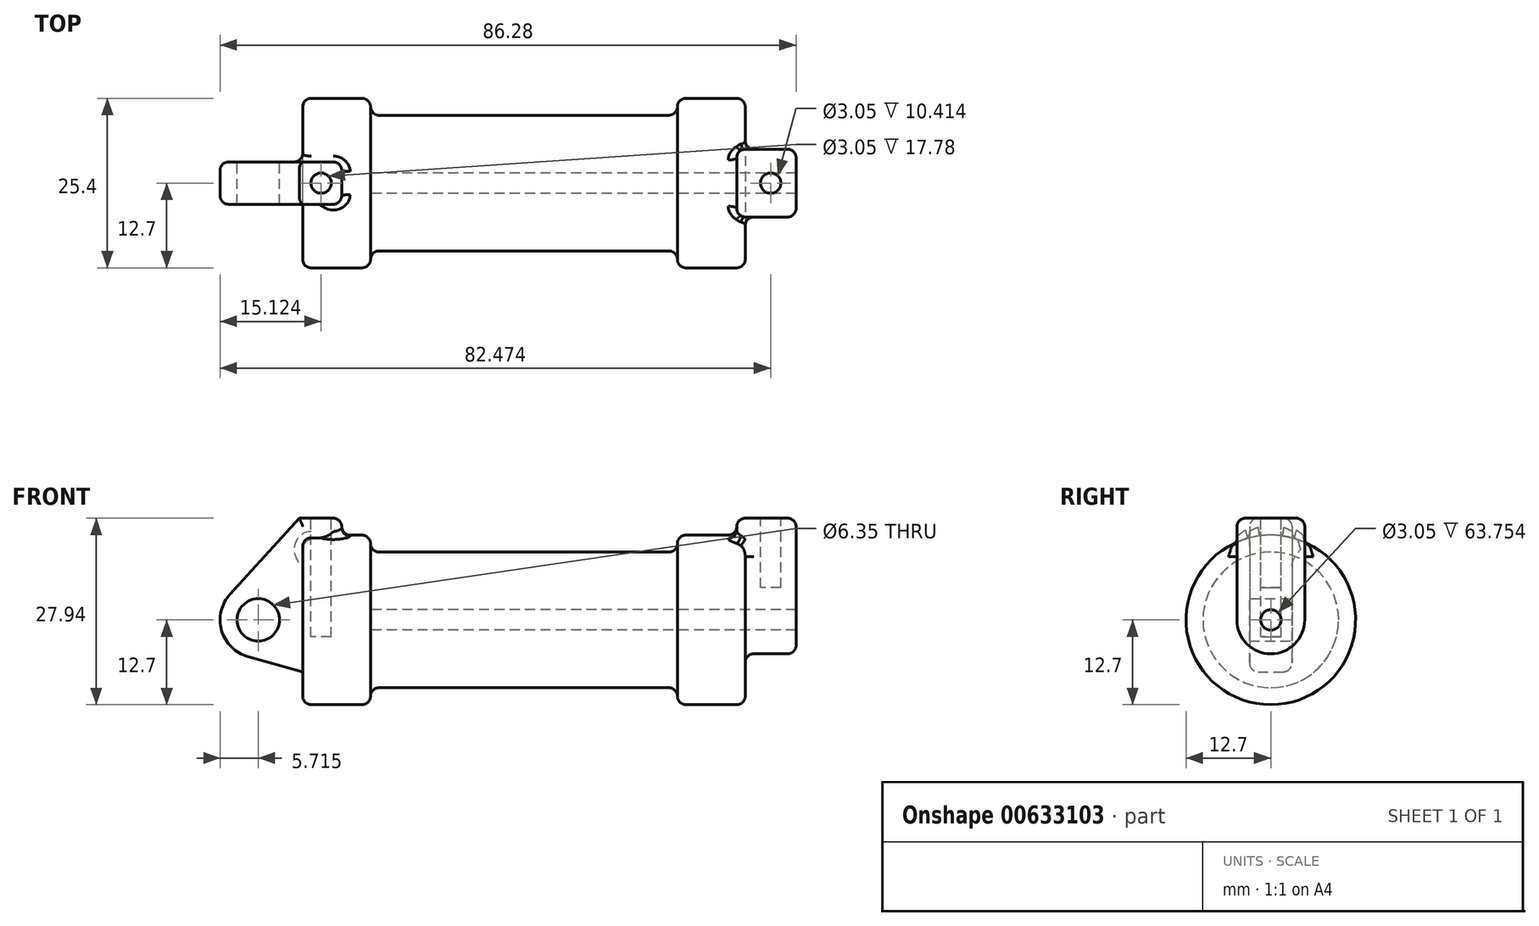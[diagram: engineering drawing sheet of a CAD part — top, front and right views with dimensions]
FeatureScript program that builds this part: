
annotation { "Feature Type Name" : "Feature", "Feature Type Description" : "" }
export const myFeature = defineFeature(function(context is Context, id is Id, definition is map)
    precondition{}
    {
        {
            var Q0;
            Q0=qCreatedBy(makeId("Front.planeOp"),FACE);
            var sketch = newSketch(context, id + "F0", { "sketchPlane" : qUnion([Q0])});
            skLineSegment(sketch, "E0", {"start": v(0, 0) * mm, "end": v(0, 12.7) * mm});
            skLineSegment(sketch, "E1", {"start": v(0, 12.7) * mm, "end": v(10.16, 12.7) * mm});
            skLineSegment(sketch, "E2", {"start": v(10.16, 12.7) * mm, "end": v(10.16, 10.16) * mm});
            skLineSegment(sketch, "E3", {"start": v(10.16, 10.16) * mm, "end": v(56.13, 10.16) * mm});
            skLineSegment(sketch, "E4", {"start": v(56.13, 10.16) * mm, "end": v(56.13, 12.7) * mm});
            skLineSegment(sketch, "E5", {"start": v(56.13, 12.7) * mm, "end": v(66.3, 12.7) * mm});
            skLineSegment(sketch, "E6", {"start": v(66.3, 12.7) * mm, "end": v(66.3, 0) * mm});
            skLineSegment(sketch, "E7", {"start": v(66.3, 0) * mm, "end": v(0, 0) * mm});
            skLineSegment(sketch, "E8", {"start": v(5.84, 15.24) * mm, "end": v(-0.5, 15.24) * mm});
            skLineSegment(sketch, "E9", {"start": v(-0.5, 15.24) * mm, "end": v(-10.88, 3.85) * mm});
            skLineSegment(sketch, "E10", {"start": v(0, 0) * mm, "end": v(-6.65, 0) * mm});
            skCircle(sketch, "E11", {"center": v(-6.65, 0) * mm, "radius": 5.72 * mm});
            skCircle(sketch, "E12", {"center": v(-6.65, 0) * mm, "radius": 3.18 * mm});
            skLineSegment(sketch, "E13", {"start": v(5.84, 15.24) * mm, "end": v(5.84, -9.4) * mm});
            skLineSegment(sketch, "E14", {"start": v(5.84, -9.4) * mm, "end": v(-8.18, -5.5) * mm});
            skSolve(sketch);
        }
        {
            var Q0;
            {var subQ0=sQuery(id+"F0.wireOp",EDGE,"E0");Q0=makeQuery(id+"F0.imprint","IMPRINT",FACE,{"disambiguationData":[TD([[makeQuery(id+"F0.imprint","IMPRINT",EDGE,{"derivedFrom":subQ0}),-1.0]])]});}
            var Q1;
            {var subQ0=sQuery(id+"F0.wireOp",EDGE,"E2");Q1=makeQuery(id+"F0.imprint","IMPRINT",FACE,{"disambiguationData":[TD([[makeQuery(id+"F0.imprint","IMPRINT",EDGE,{"derivedFrom":subQ0}),-1.0]])]});}
            var Q2;
            Q2=sQuery(id+"F0.wireOp",EDGE,"E7");
            revolve(context, id + "F1", {"entities" : qUnion([Q0, Q1]), "axis" : qUnion([Q2]), "revolveType" : RevolveType.FULL});
        }
        {
            var Q0;
            Q0=makeQuery(id+"F1.opRevolve","SWEPT_FACE",FACE,{"disambiguationData":[OSD([sQuery(id+"F0.wireOp",EDGE,"E6")])]});
            var sketch = newSketch(context, id + "F2", { "sketchPlane" : qUnion([Q0])});
            skCircle(sketch, "E15", {"center": v(0, 0) * mm, "radius": 1.52 * mm});
            skCircle(sketch, "E16", {"center": v(0, 0) * mm, "radius": 5.08 * mm});
            skLineSegment(sketch, "E17", {"start": v(5.08, 0) * mm, "end": v(5.08, 15.24) * mm});
            skLineSegment(sketch, "E18", {"start": v(-5.08, 0) * mm, "end": v(-5.08, 15.24) * mm});
            skLineSegment(sketch, "E19", {"start": v(-5.08, 15.24) * mm, "end": v(5.08, 15.24) * mm});
            skSolve(sketch);
        }
        {
            var Q0;
            Q0 = qSketchRegion(id + "F2", true);
            extrude(context, id + "F3", {"entities" : qUnion([Q0]), "operationType" : NewBodyOperationType.ADD, "depth" : 7.62 * mm, "offsetDistance" : 25.4 * mm, "hasSecondDirection" : true, "secondDirectionOppositeDirection" : true, "secondDirectionDepth" : 1.27 * mm});
        }
        {
            var Q0;
            Q0=makeQuery(id+"F2.imprint","IMPRINT",FACE,{"disambiguationData":[TD([[makeQuery(id+"F2.imprint","IMPRINT",EDGE,{"derivedFrom":sQuery(id+"F2.wireOp",EDGE,"E15")}),1.0]])]});
            var Q1;
            Q1=makeQuery(id+"F1.opRevolve","SWEPT_FACE",FACE,{"disambiguationData":[OSD([sQuery(id+"F0.wireOp",EDGE,"E2")])]});
            extrude(context, id + "F4", {"entities" : qUnion([Q0]), "operationType" : NewBodyOperationType.REMOVE, "endBound" : BoundingType.UP_TO_SURFACE, "oppositeDirection" : true, "depth" : 25.4 * mm, "endBoundEntityFace" : qUnion([Q1]), "offsetDistance" : 25.4 * mm});
        }
        {
            var Q0;
            Q0=makeQuery(id+"F3.opExtrude","SWEPT_FACE",FACE,{"disambiguationData":[OSD([sQuery(id+"F2.wireOp",EDGE,"E19")])]});
            var sketch = newSketch(context, id + "F5", { "sketchPlane" : qUnion([Q0])});
            skCircle(sketch, "E20", {"center": v(70.1, 0) * mm, "radius": 1.52 * mm});
            skSolve(sketch);
        }
        {
            var Q0;
            Q0 = qSketchRegion(id + "F5", true);
            extrude(context, id + "F6", {"entities" : qUnion([Q0]), "operationType" : NewBodyOperationType.REMOVE, "oppositeDirection" : true, "depth" : 10.4 * mm, "offsetDistance" : 25.4 * mm});
        }
        {
            var Q0;
            {var subQ0=sQuery(id+"F0.wireOp",EDGE,"E0");Q0=makeQuery(id+"F0.imprint","IMPRINT",FACE,{"disambiguationData":[TD([[makeQuery(id+"F0.imprint","IMPRINT",EDGE,{"derivedFrom":subQ0}),-1.0]])]});}
            var Q1;
            {var subQ1=sQuery(id+"F0.wireOp",EDGE,"E0");Q1=makeQuery(id+"F0.imprint","IMPRINT",FACE,{"disambiguationData":[TD([[makeQuery(id+"F0.imprint","IMPRINT",EDGE,{"derivedFrom":subQ1}),1.0]])]});}
            var Q2;
            {var subQ0=sQuery(id+"F0.wireOp",EDGE,"E14");Q2=makeQuery(id+"F0.imprint","IMPRINT",FACE,{"disambiguationData":[TD([[makeQuery(id+"F0.imprint","IMPRINT",EDGE,{"derivedFrom":subQ0}),-1.0]])]});}
            var Q3;
            {var subQ5=sQuery(id+"F0.wireOp",EDGE,"E12");Q3=makeQuery(id+"F0.imprint","IMPRINT",FACE,{"disambiguationData":[TD([[makeQuery(id+"F0.imprint","IMPRINT",EDGE,{"derivedFrom":subQ5}),-1.0]])]});}
            extrude(context, id + "F7", {"entities" : qUnion([Q0, Q1, Q2, Q3]), "operationType" : NewBodyOperationType.ADD, "endBound" : BoundingType.SYMMETRIC, "depth" : 6.35 * mm, "offsetDistance" : 25.4 * mm});
        }
        {
            var Q0;
            Q0=makeQuery(id+"F7.opExtrude","SWEPT_FACE",FACE,{"disambiguationData":[OSD([sQuery(id+"F0.wireOp",EDGE,"E8")])]});
            var sketch = newSketch(context, id + "F8", { "sketchPlane" : qUnion([Q0])});
            skSolve(sketch);
        }
        {
            var Q0;
            {var subQ0=sQuery(id+"F0.wireOp",EDGE,"E8");Q0=makeQuery(id+"F8.imprint","IMPRINT",FACE,{"disambiguationData":[TD([[makeQuery(id+"F8.imprint","IMPRINT",EDGE,{"derivedFrom":makeQuery(id+"F7.opExtrude","CAP_EDGE",EDGE,{"disambiguationData":[OSD([subQ0])],"isStart":true})}),1.0]])]});}
            var sketch = newSketch(context, id + "F9", { "sketchPlane" : qUnion([Q0])});
            skCircle(sketch, "E21", {"center": v(2.75, 0) * mm, "radius": 1.52 * mm});
            skSolve(sketch);
        }
        {
            var Q0;
            Q0=makeQuery(id+"F9.imprint","IMPRINT",FACE,{"disambiguationData":[TD([[makeQuery(id+"F9.imprint","IMPRINT",EDGE,{"derivedFrom":sQuery(id+"F9.wireOp",EDGE,"E21")}),1.0]])]});
            extrude(context, id + "F10", {"entities" : qUnion([Q0]), "operationType" : NewBodyOperationType.REMOVE, "oppositeDirection" : true, "depth" : 17.78 * mm, "offsetDistance" : 25.4 * mm});
        }
        {
            var Q0;
            Q0=makeQuery(id+"F1.opRevolve","SWEPT_EDGE",EDGE,{"disambiguationData":[OSD([sQuery(id+"F0.wireOp",EDGE,"E1"),sQuery(id+"F0.wireOp",EDGE,"E2")])]});
            var Q1;
            Q1=makeQuery(id+"F1.opRevolve","SWEPT_EDGE",EDGE,{"disambiguationData":[OSD([sQuery(id+"F0.wireOp",EDGE,"E2"),sQuery(id+"F0.wireOp",EDGE,"E3")])]});
            var Q2;
            Q2=makeQuery(id+"F1.opRevolve","SWEPT_EDGE",EDGE,{"disambiguationData":[OSD([sQuery(id+"F0.wireOp",EDGE,"E3"),sQuery(id+"F0.wireOp",EDGE,"E4")])]});
            var Q3;
            Q3=makeQuery(id+"F1.opRevolve","SWEPT_EDGE",EDGE,{"disambiguationData":[OSD([sQuery(id+"F0.wireOp",EDGE,"E4"),sQuery(id+"F0.wireOp",EDGE,"E5")])]});
            var Q4;
            Q4=makeQuery(id+"F1.opRevolve","SWEPT_EDGE",EDGE,{"disambiguationData":[OSD([sQuery(id+"F0.wireOp",EDGE,"E0"),sQuery(id+"F0.wireOp",EDGE,"E1")])]});
            var Q5;
            Q5=makeQuery(id+"F1.opRevolve","SWEPT_EDGE",EDGE,{"disambiguationData":[OSD([sQuery(id+"F0.wireOp",EDGE,"E5"),sQuery(id+"F0.wireOp",EDGE,"E6")])]});
            var Q6;
            Q6=makeQuery(id+"F7.boolean.opBoolean","INTERSECT",EDGE,{"derivedFrom":[makeQuery(id+"F1.opRevolve","SWEPT_FACE",FACE,{"disambiguationData":[OSD([sQuery(id+"F0.wireOp",EDGE,"E1")])]}),makeQuery(id+"F7.opExtrude","CAP_FACE",FACE,{"disambiguationData":[OSD([sQuery(id+"F0.wireOp",EDGE,"E8"),sQuery(id+"F0.wireOp",EDGE,"E9"),sQuery(id+"F0.wireOp",EDGE,"E11"),sQuery(id+"F0.wireOp",EDGE,"E12"),sQuery(id+"F0.wireOp",EDGE,"E13"),sQuery(id+"F0.wireOp",EDGE,"E14")])],"isStart":true})]});
            var Q7;
            Q7=makeQuery(id+"F7.opExtrude","CAP_EDGE",EDGE,{"disambiguationData":[OSD([sQuery(id+"F0.wireOp",EDGE,"E9")])],"isStart":true});
            var Q8;
            Q8=makeQuery(id+"F7.opExtrude","CAP_EDGE",EDGE,{"disambiguationData":[OSD([sQuery(id+"F0.wireOp",EDGE,"E8")])],"isStart":true});
            var Q9;
            Q9=makeQuery(id+"F7.opExtrude","CAP_EDGE",EDGE,{"disambiguationData":[OSD([sQuery(id+"F0.wireOp",EDGE,"E9")])],"isStart":false});
            var Q10;
            Q10=makeQuery(id+"F7.opExtrude","CAP_EDGE",EDGE,{"disambiguationData":[OSD([sQuery(id+"F0.wireOp",EDGE,"E8")])],"isStart":false});
            var Q11;
            Q11=makeQuery(id+"F7.opExtrude","SWEPT_EDGE",EDGE,{"disambiguationData":[OSD([sQuery(id+"F0.wireOp",EDGE,"E8"),sQuery(id+"F0.wireOp",EDGE,"E13")])]});
            var Q12;
            Q12=makeQuery(id+"F7.boolean.opBoolean","INTERSECT",EDGE,{"derivedFrom":[makeQuery(id+"F1.opRevolve","SWEPT_FACE",FACE,{"disambiguationData":[OSD([sQuery(id+"F0.wireOp",EDGE,"E1")])]}),makeQuery(id+"F7.opExtrude","SWEPT_FACE",FACE,{"disambiguationData":[OSD([sQuery(id+"F0.wireOp",EDGE,"E13")])]})]});
            var Q13;
            Q13=makeQuery(id+"F7.opExtrude","CAP_EDGE",EDGE,{"disambiguationData":[OSD([sQuery(id+"F0.wireOp",EDGE,"E13")])],"isStart":false});
            var Q14;
            Q14=makeQuery(id+"F7.opExtrude","CAP_EDGE",EDGE,{"disambiguationData":[OSD([sQuery(id+"F0.wireOp",EDGE,"E13")])],"isStart":true});
            fillet(context, id + "F11", {"entities" : qUnion([Q0, Q1, Q2, Q3, Q4, Q5, Q6, Q7, Q8, Q9, Q10, Q11, Q12, Q13, Q14]), "radius" : 1.27 * mm, "tangentPropagation" : true, "allowEdgeOverflow" : false});
        }
        {
            var Q0;
            Q0=makeQuery(id+"F3.opExtrude","CAP_EDGE",EDGE,{"disambiguationData":[OSD([sQuery(id+"F2.wireOp",EDGE,"E17")])],"isStart":true});
            var Q1;
            Q1=makeQuery(id+"F3.opExtrude","CAP_EDGE",EDGE,{"disambiguationData":[OSD([sQuery(id+"F2.wireOp",EDGE,"E18")])],"isStart":true});
            var Q2;
            Q2=makeQuery(id+"F3.boolean.opBoolean","INTERSECT",EDGE,{"derivedFrom":[makeQuery(id+"F1.opRevolve","SWEPT_FACE",FACE,{"disambiguationData":[OSD([sQuery(id+"F0.wireOp",EDGE,"E5")])]}),makeQuery(id+"F3.opExtrude","CAP_FACE",FACE,{"disambiguationData":[OSD([sQuery(id+"F2.wireOp",EDGE,"E15"),sQuery(id+"F2.wireOp",EDGE,"E16"),sQuery(id+"F2.wireOp",EDGE,"E17"),sQuery(id+"F2.wireOp",EDGE,"E18"),sQuery(id+"F2.wireOp",EDGE,"E19")])],"isStart":true})]});
            var Q3;
            Q3=makeQuery(id+"F3.opExtrude","CAP_EDGE",EDGE,{"disambiguationData":[OSD([sQuery(id+"F2.wireOp",EDGE,"E19")])],"isStart":true});
            var Q4;
            Q4=makeQuery(id+"F3.boolean.opBoolean","INTERSECT",EDGE,{"derivedFrom":[makeQuery(id+"F1.opRevolve","SWEPT_FACE",FACE,{"disambiguationData":[OSD([sQuery(id+"F0.wireOp",EDGE,"E6")])]}),makeQuery(id+"F3.opExtrude","SWEPT_FACE",FACE,{"disambiguationData":[OSD([sQuery(id+"F2.wireOp",EDGE,"E18")])]})]});
            var Q5;
            Q5=makeQuery(id+"F3.opExtrude","CAP_EDGE",EDGE,{"disambiguationData":[OSD([sQuery(id+"F2.wireOp",EDGE,"E18")])],"isStart":false});
            var Q6;
            Q6=makeQuery(id+"F3.opExtrude","SWEPT_EDGE",EDGE,{"disambiguationData":[OSD([sQuery(id+"F2.wireOp",EDGE,"E17"),sQuery(id+"F2.wireOp",EDGE,"E19")])]});
            var Q7;
            Q7=makeQuery(id+"F3.opExtrude","CAP_EDGE",EDGE,{"disambiguationData":[OSD([sQuery(id+"F2.wireOp",EDGE,"E19")])],"isStart":false});
            var Q8;
            Q8=makeQuery(id+"F3.opExtrude","SWEPT_EDGE",EDGE,{"disambiguationData":[OSD([sQuery(id+"F2.wireOp",EDGE,"E18"),sQuery(id+"F2.wireOp",EDGE,"E19")])]});
            fillet(context, id + "F12", {"entities" : qUnion([Q0, Q1, Q2, Q3, Q4, Q5, Q6, Q7, Q8]), "radius" : 1.27 * mm, "tangentPropagation" : true, "allowEdgeOverflow" : false});
        }
    });
